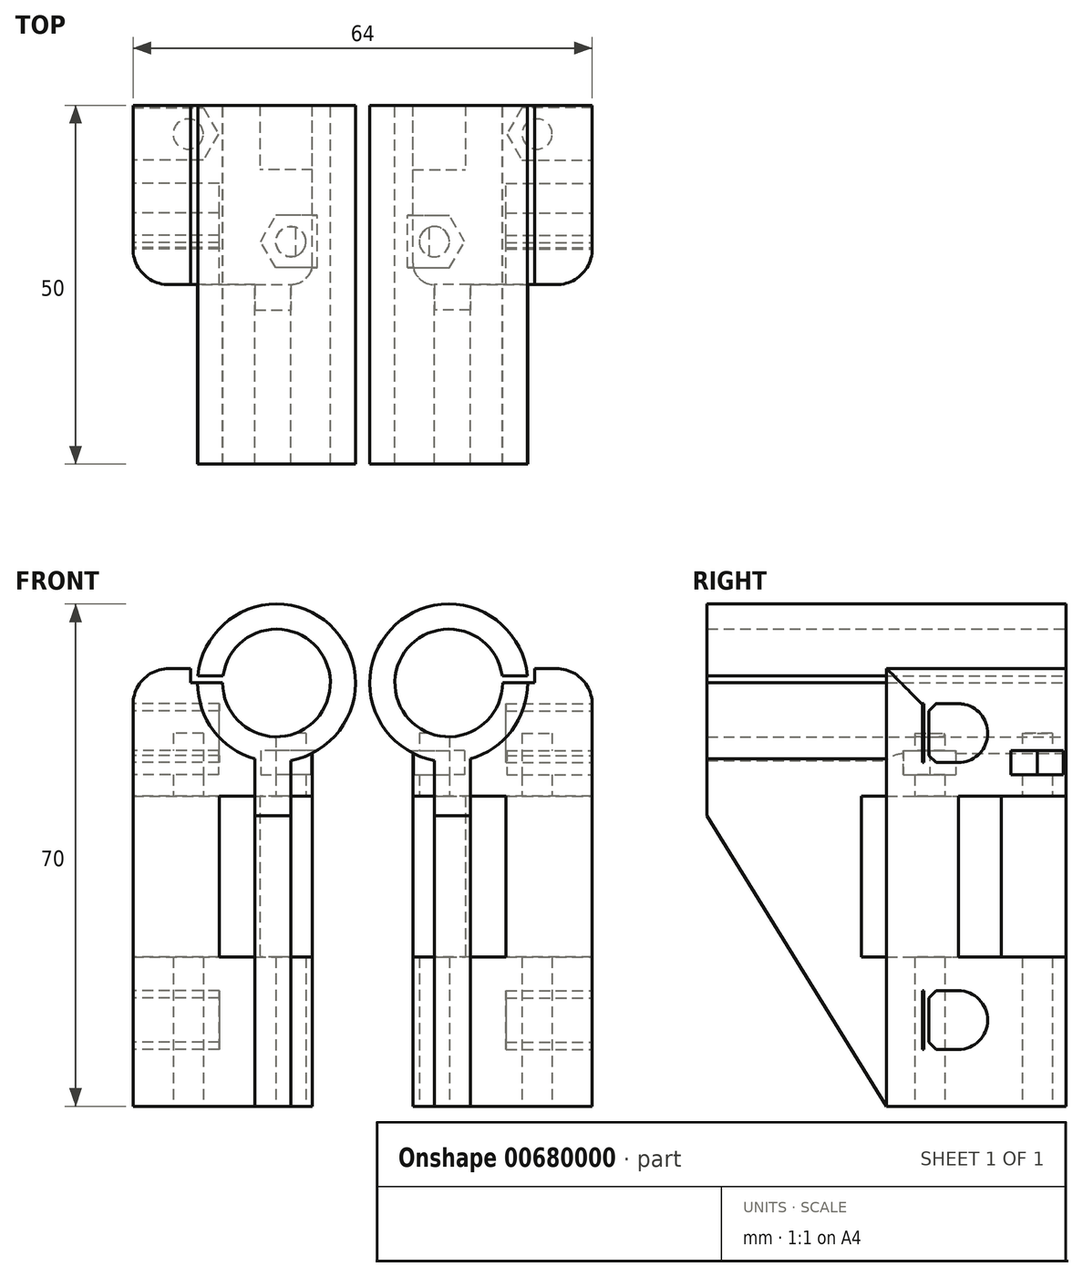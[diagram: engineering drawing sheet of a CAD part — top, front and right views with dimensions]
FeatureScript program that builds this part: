
annotation { "Feature Type Name" : "Feature", "Feature Type Description" : "" }
export const myFeature = defineFeature(function(context is Context, id is Id, definition is map)
    precondition{}
    {
        {
            var Q0;
            Q0=qCreatedBy(makeId("Front.planeOp"),FACE);
            var sketch = newSketch(context, id + "F0", { "sketchPlane" : qUnion([Q0])});
            skCircle(sketch, "E0", {"center": v(12, -12) * mm, "radius": 7.5 * mm});
            skCircle(sketch, "E1", {"center": v(12, -12) * mm, "radius": 11 * mm});
            skLineSegment(sketch, "E2", {"start": v(12, -12) * mm, "end": v(23, -12) * mm});
            skPoint(sketch, "E3.rect.middle", {"position": v(32, -10) * mm});
            skLineSegment(sketch, "E4", {"start": v(32, -10) * mm, "end": v(24, -10) * mm});
            skLineSegment(sketch, "E5", {"start": v(23, -12) * mm, "end": v(24, -12) * mm});
            skLineSegment(sketch, "E6", {"start": v(24, -12) * mm, "end": v(24, -10) * mm});
            skLineSegment(sketch, "E7", {"start": v(12, -12) * mm, "end": v(12, -11) * mm});
            skLineSegment(sketch, "E8", {"start": v(12, -11) * mm, "end": v(22.95, -11) * mm});
            skLineSegment(sketch, "E9", {"start": v(32, -10) * mm, "end": v(32, -71) * mm});
            skLineSegment(sketch, "E10", {"start": v(32, -71) * mm, "end": v(7, -71) * mm});
            skLineSegment(sketch, "E11", {"start": v(7, -71) * mm, "end": v(7, -23) * mm});
            skLineSegment(sketch, "E12", {"start": v(7, -23) * mm, "end": v(12, -23) * mm, "construction": true});
            skLineSegment(sketch, "E13", {"start": v(7, -23) * mm, "end": v(7, -21.8) * mm});
            skSolve(sketch);
        }
        {
            var Q0;
            {var subQ0=sQuery(id+"F0.wireOp",EDGE,"E2");var subQ1=sQuery(id+"F0.wireOp",EDGE,"E0");var subQ2=makeQuery(id+"F0.imprint","INTERSECT",VERTEX,{"derivedFrom":[subQ1,subQ0]});Q0=makeQuery(id+"F0.imprint","IMPRINT",FACE,{"disambiguationData":[TD([[makeQuery(id+"F0.imprint","IMPRINT",EDGE,{"disambiguationData":[TD([[subQ2,1.0]])],"derivedFrom":subQ1}),-1.0]])]});}
            extrude(context, id + "F1", {"entities" : qUnion([Q0]), "depth" : 50 * mm});
        }
        {
            var Q0;
            Q0=makeQuery(id+"F0.imprint","IMPRINT",FACE,{"disambiguationData":[TD([[makeQuery(id+"F0.imprint","IMPRINT",EDGE,{"derivedFrom":sQuery(id+"F0.wireOp",EDGE,"E4")}),1.0]])]});
            extrude(context, id + "F2", {"entities" : qUnion([Q0]), "operationType" : NewBodyOperationType.ADD, "depth" : 25 * mm});
        }
        {
            var Q0;
            Q0=makeQuery(id+"F2.opExtrude","SWEPT_FACE",FACE,{"disambiguationData":[OSD([sQuery(id+"F0.wireOp",EDGE,"E9")])]});
            var sketch = newSketch(context, id + "F3", { "sketchPlane" : qUnion([Q0])});
            skLineSegment(sketch, "E14", {"start": v(0, -71) * mm, "end": v(-15, -71) * mm, "construction": true});
            skLineSegment(sketch, "E15", {"start": v(-15, -71) * mm, "end": v(-15, -59) * mm, "construction": true});
            skLineSegment(sketch, "E16", {"start": v(-15, -59) * mm, "end": v(-15, -19) * mm, "construction": true});
            skCircle(sketch, "E17", {"center": v(-15, -59) * mm, "radius": 4.1 * mm});
            skCircle(sketch, "E18", {"center": v(-15, -59) * mm, "radius": 7.5 * mm, "construction": true});
            skCircle(sketch, "E19", {"center": v(-15, -19) * mm, "radius": 7.5 * mm, "construction": true});
            skLineSegment(sketch, "E20", {"start": v(-15, -39) * mm, "end": v(-16.5, -39) * mm, "construction": true});
            skLineSegment(sketch, "E21", {"start": v(-16.5, -39) * mm, "end": v(-16.5, -44.4) * mm, "construction": true});
            skCircle(sketch, "E22", {"center": v(-16.5, -44.4) * mm, "radius": 3 * mm, "construction": true});
            skCircle(sketch, "E23.0.MirrorC", {"center": v(-16.5, -33.6) * mm, "radius": 3 * mm, "construction": true});
            skLineSegment(sketch, "E24", {"start": v(-15, -54.9) * mm, "end": v(-20, -54.9) * mm, "construction": true});
            skLineSegment(sketch, "E25", {"start": v(-15, -63.1) * mm, "end": v(-20, -63.1) * mm, "construction": true});
            skLineSegment(sketch, "E26", {"start": v(-19.1, -54.9) * mm, "end": v(-19.1, -63.1) * mm});
            skLineSegment(sketch, "E27", {"start": v(-19.1, -55.9) * mm, "end": v(-18.1, -54.9) * mm});
            skLineSegment(sketch, "E28", {"start": v(-18.1, -54.9) * mm, "end": v(-15, -54.9) * mm});
            skLineSegment(sketch, "E29", {"start": v(-15, -63.1) * mm, "end": v(-18.1, -63.1) * mm});
            skLineSegment(sketch, "E30", {"start": v(-18.1, -63.1) * mm, "end": v(-19.1, -62.1) * mm});
            skLineSegment(sketch, "E31.bottom", {"start": v(-19.8, -54.9) * mm, "end": v(-20, -54.9) * mm});
            skLineSegment(sketch, "E31.top", {"start": v(-19.8, -63.1) * mm, "end": v(-20, -63.1) * mm});
            skLineSegment(sketch, "E31.left", {"start": v(-19.8, -54.9) * mm, "end": v(-19.8, -63.1) * mm});
            skLineSegment(sketch, "E31.right", {"start": v(-20, -54.9) * mm, "end": v(-20, -63.1) * mm});
            skLineSegment(sketch, "E32", {"start": v(-15, -39) * mm, "end": v(5.06, -39) * mm, "construction": true});
            skLineSegment(sketch, "E33.MirrorCS", {"start": v(-19.8, -23.1) * mm, "end": v(-20, -23.1) * mm});
            skLineSegment(sketch, "E34.MirrorCS", {"start": v(-19.8, -14.9) * mm, "end": v(-20, -14.9) * mm});
            skLineSegment(sketch, "E35.MirrorCS", {"start": v(-19.1, -22.1) * mm, "end": v(-18.1, -23.1) * mm});
            skLineSegment(sketch, "E36.MirrorCS", {"start": v(-18.1, -14.9) * mm, "end": v(-19.1, -15.9) * mm});
            skLineSegment(sketch, "E37.MirrorCS", {"start": v(-15, -14.9) * mm, "end": v(-20, -14.9) * mm, "construction": true});
            skLineSegment(sketch, "E38.MirrorCS", {"start": v(-15, -23.1) * mm, "end": v(-20, -23.1) * mm, "construction": true});
            skLineSegment(sketch, "E39.MirrorCS", {"start": v(-18.1, -23.1) * mm, "end": v(-15, -23.1) * mm});
            skLineSegment(sketch, "E40.MirrorCS", {"start": v(-19.8, -23.1) * mm, "end": v(-19.8, -14.9) * mm});
            skLineSegment(sketch, "E41.MirrorCS", {"start": v(-20, -23.1) * mm, "end": v(-20, -14.9) * mm});
            skLineSegment(sketch, "E42.MirrorCS", {"start": v(-19.1, -23.1) * mm, "end": v(-19.1, -14.9) * mm});
            skCircle(sketch, "E43.MirrorC", {"center": v(-15, -19) * mm, "radius": 4.1 * mm});
            skLineSegment(sketch, "E44.MirrorCS", {"start": v(-15, -14.9) * mm, "end": v(-18.1, -14.9) * mm});
            skSolve(sketch);
        }
        {
            var Q0;
            Q0=makeQuery(id+"F2.opExtrude","SWEPT_FACE",FACE,{"disambiguationData":[OSD([sQuery(id+"F0.wireOp",EDGE,"E10")])]});
            var sketch = newSketch(context, id + "F4", { "sketchPlane" : qUnion([Q0])});
            skLineSegment(sketch, "E45", {"start": v(0, 0) * mm, "end": v(0, 19) * mm, "construction": true});
            skLineSegment(sketch, "E46", {"start": v(0, 19) * mm, "end": v(10, 19) * mm, "construction": true});
            skLineSegment(sketch, "E47", {"start": v(10, 19) * mm, "end": v(10, 4) * mm, "construction": true});
            skLineSegment(sketch, "E48", {"start": v(10, 4) * mm, "end": v(24.3, 4) * mm, "construction": true});
            skCircle(sketch, "E49", {"center": v(10, 19) * mm, "radius": 2.1 * mm});
            skCircle(sketch, "E50", {"center": v(10, 19) * mm, "radius": 6.5 * mm, "construction": true});
            skCircle(sketch, "E51", {"center": v(24.3, 4) * mm, "radius": 2.1 * mm});
            skCircle(sketch, "E52", {"center": v(24.3, 4) * mm, "radius": 6.5 * mm, "construction": true});
            skLineSegment(sketch, "E53", {"start": v(14.3, 0) * mm, "end": v(14.3, 9) * mm});
            skLineSegment(sketch, "E54", {"start": v(20, 15) * mm, "end": v(32, 15) * mm});
            skLineSegment(sketch, "E55", {"start": v(32, 15) * mm, "end": v(32, 4) * mm});
            skLineSegment(sketch, "E56", {"start": v(24.3, 4) * mm, "end": v(24.3, 0) * mm, "construction": true});
            skLineSegment(sketch, "E57", {"start": v(24.3, 0) * mm, "end": v(14.3, 0) * mm});
            skLineSegment(sketch, "E58", {"start": v(20, 25) * mm, "end": v(20, 15) * mm});
            skLineSegment(sketch, "E59", {"start": v(7, 9) * mm, "end": v(14.3, 9) * mm});
            skLineSegment(sketch, "E60", {"start": v(7, 9) * mm, "end": v(7, 25) * mm});
            skLineSegment(sketch, "E61", {"start": v(7, 25) * mm, "end": v(20, 25) * mm});
            skLineSegment(sketch, "E62", {"start": v(24.3, 0) * mm, "end": v(32, 0) * mm});
            skLineSegment(sketch, "E63", {"start": v(32, 0) * mm, "end": v(32, 4) * mm});
            skLineSegment(sketch, "E64", {"start": v(32, 4) * mm, "end": v(24.3, 4) * mm, "construction": true});
            skSolve(sketch);
        }
        {
            var Q0;
            Q0=makeQuery(id+"F4.imprint","IMPRINT",FACE,{"disambiguationData":[TD([[makeQuery(id+"F4.imprint","IMPRINT",EDGE,{"derivedFrom":sQuery(id+"F4.wireOp",EDGE,"E49")}),-1.0]])]});
            extrude(context, id + "F5", {"entities" : qUnion([Q0]), "operationType" : NewBodyOperationType.REMOVE, "oppositeDirection" : true, "depth" : 12 * mm + (40 * mm + 22.4 * mm) * .5});
        }
        {
            var Q0;
            Q0=makeQuery(id+"F4.imprint","IMPRINT",FACE,{"disambiguationData":[TD([[makeQuery(id+"F4.imprint","IMPRINT",EDGE,{"derivedFrom":sQuery(id+"F4.wireOp",EDGE,"E49")}),-1.0]])]});
            extrude(context, id + "F6", {"entities" : qUnion([Q0]), "operationType" : NewBodyOperationType.ADD, "oppositeDirection" : true, "depth" : 12 * mm + (40 * mm - 22.4 * mm) * .5});
        }
        {
            var Q0;
            Q0=makeQuery(id+"F4.imprint","IMPRINT",FACE,{"disambiguationData":[TD([[makeQuery(id+"F4.imprint","IMPRINT",EDGE,{"derivedFrom":sQuery(id+"F4.wireOp",EDGE,"E49")}),1.0]])]});
            var Q1;
            Q1=makeQuery(id+"F4.imprint","IMPRINT",FACE,{"disambiguationData":[TD([[makeQuery(id+"F4.imprint","IMPRINT",EDGE,{"derivedFrom":sQuery(id+"F4.wireOp",EDGE,"E51")}),1.0]])]});
            extrude(context, id + "F7", {"entities" : qUnion([Q0, Q1]), "operationType" : NewBodyOperationType.REMOVE, "oppositeDirection" : true, "depth" : 12 * mm + 40 * mm});
        }
        {
            var Q0;
            Q0=makeQuery(id+"F5.boolean.opBoolean","COPY",FACE,{"derivedFrom":makeQuery(id+"F5.opExtrude","CAP_FACE",FACE,{"disambiguationData":[OSD([sQuery(id+"F4.wireOp",EDGE,"E49"),sQuery(id+"F4.wireOp",EDGE,"E51"),sQuery(id+"F4.wireOp",EDGE,"E53"),sQuery(id+"F4.wireOp",EDGE,"E54"),sQuery(id+"F4.wireOp",EDGE,"E55"),sQuery(id+"F4.wireOp",EDGE,"E57"),sQuery(id+"F4.wireOp",EDGE,"E58"),sQuery(id+"F4.wireOp",EDGE,"E59"),sQuery(id+"F4.wireOp",EDGE,"E60"),sQuery(id+"F4.wireOp",EDGE,"E61"),sQuery(id+"F4.wireOp",EDGE,"E62"),sQuery(id+"F4.wireOp",EDGE,"E63")])],"isStart":false})});
            var sketch = newSketch(context, id + "F8", { "sketchPlane" : qUnion([Q0])});
            skCircle(sketch, "E65.cCircle", {"center": v(24.3, 4) * mm, "radius": 3.65 * mm, "construction": true});
            skLineSegment(sketch, "E65.0", {"start": v(28.51, 4) * mm, "end": v(26.4, 0.35) * mm, "construction": true});
            skLineSegment(sketch, "E65.1", {"start": v(26.4, 0.35) * mm, "end": v(22.2, 0.35) * mm});
            skLineSegment(sketch, "E65.2", {"start": v(22.2, 0.35) * mm, "end": v(20.09, 4) * mm});
            skLineSegment(sketch, "E65.3", {"start": v(20.09, 4) * mm, "end": v(22.2, 7.65) * mm});
            skLineSegment(sketch, "E65.4", {"start": v(22.2, 7.65) * mm, "end": v(26.4, 7.65) * mm});
            skLineSegment(sketch, "E65.5", {"start": v(26.4, 7.65) * mm, "end": v(28.51, 4) * mm, "construction": true});
            skPoint(sketch, "E65.0.midPoint", {"position": v(27.46, 2.18) * mm});
            skCircle(sketch, "E66.cCircle", {"center": v(10, 19) * mm, "radius": 3.65 * mm, "construction": true});
            skLineSegment(sketch, "E66.0", {"start": v(14.21, 19) * mm, "end": v(12.1, 15.35) * mm});
            skLineSegment(sketch, "E66.1", {"start": v(12.1, 15.35) * mm, "end": v(7.9, 15.35) * mm});
            skLineSegment(sketch, "E66.2", {"start": v(7.9, 15.35) * mm, "end": v(5.79, 19) * mm, "construction": true});
            skLineSegment(sketch, "E66.3", {"start": v(5.79, 19) * mm, "end": v(7.9, 22.65) * mm, "construction": true});
            skLineSegment(sketch, "E66.4", {"start": v(7.9, 22.65) * mm, "end": v(12.1, 22.65) * mm});
            skLineSegment(sketch, "E66.5", {"start": v(12.1, 22.65) * mm, "end": v(14.21, 19) * mm});
            skPoint(sketch, "E66.0.midPoint", {"position": v(13.16, 17.18) * mm});
            skLineSegment(sketch, "E67", {"start": v(7.9, 22.65) * mm, "end": v(7, 22.65) * mm});
            skLineSegment(sketch, "E68", {"start": v(7, 22.65) * mm, "end": v(7, 15.35) * mm});
            skLineSegment(sketch, "E69", {"start": v(7, 15.35) * mm, "end": v(7.9, 15.35) * mm});
            skLineSegment(sketch, "E70", {"start": v(26.4, 7.65) * mm, "end": v(32, 7.65) * mm});
            skLineSegment(sketch, "E71", {"start": v(32, 7.65) * mm, "end": v(32, 0.35) * mm});
            skLineSegment(sketch, "E72", {"start": v(32, 0.35) * mm, "end": v(26.4, 0.35) * mm});
            skLineSegment(sketch, "E73", {"start": v(7, 22.65) * mm, "end": v(-3, 22.65) * mm});
            skLineSegment(sketch, "E74", {"start": v(-3, 22.65) * mm, "end": v(-3, 15.35) * mm});
            skLineSegment(sketch, "E75", {"start": v(-3, 15.35) * mm, "end": v(7, 15.35) * mm});
            skSolve(sketch);
        }
        {
            var Q0;
            Q0=makeQuery(id+"F8.imprint","IMPRINT",FACE,{"disambiguationData":[TD([[makeQuery(id+"F8.imprint","IMPRINT",EDGE,{"derivedFrom":sQuery(id+"F8.wireOp",EDGE,"E65.1")}),-1.0]])]});
            var Q1;
            Q1=makeQuery(id+"F8.imprint","IMPRINT",FACE,{"disambiguationData":[TD([[makeQuery(id+"F8.imprint","IMPRINT",EDGE,{"derivedFrom":sQuery(id+"F8.wireOp",EDGE,"E66.0")}),-1.0]])]});
            var Q2;
            Q2=makeQuery(id+"F8.imprint","IMPRINT",FACE,{"disambiguationData":[TD([[makeQuery(id+"F8.imprint","IMPRINT",EDGE,{"derivedFrom":sQuery(id+"F8.wireOp",EDGE,"E68")}),-1.0]])]});
            extrude(context, id + "F9", {"entities" : qUnion([Q0, Q1, Q2]), "operationType" : NewBodyOperationType.REMOVE, "oppositeDirection" : true, "depth" : 6.4 * mm});
        }
        {
            var Q0;
            Q0=makeQuery(id+"F8.imprint","IMPRINT",FACE,{"disambiguationData":[TD([[makeQuery(id+"F8.imprint","IMPRINT",EDGE,{"derivedFrom":sQuery(id+"F8.wireOp",EDGE,"E66.0")}),-1.0]])]});
            var Q1;
            Q1=makeQuery(id+"F8.imprint","IMPRINT",FACE,{"disambiguationData":[TD([[makeQuery(id+"F8.imprint","IMPRINT",EDGE,{"derivedFrom":sQuery(id+"F8.wireOp",EDGE,"E65.1")}),-1.0]])]});
            extrude(context, id + "F10", {"entities" : qUnion([Q0, Q1]), "operationType" : NewBodyOperationType.ADD, "oppositeDirection" : true, "depth" : 3 * mm});
        }
        {
            var Q0;
            Q0=qSketchRegion(id+"F3",true);
            extrude(context, id + "F11", {"entities" : qUnion([Q0]), "operationType" : NewBodyOperationType.REMOVE, "oppositeDirection" : true, "depth" : 12 * mm});
        }
        {
            var Q0;
            Q0=makeQuery(id+"F10.boolean.opBoolean","MERGE",FACE,{"derivedFrom":[makeQuery(id+"F6.boolean.opBoolean","MERGE",FACE,{"derivedFrom":[makeQuery(id+"F2.opExtrude","SWEPT_FACE",FACE,{"disambiguationData":[OSD([sQuery(id+"F0.wireOp",EDGE,"E11"),sQuery(id+"F0.wireOp",EDGE,"E13")])]}),makeQuery(id+"F6.opExtrude","SWEPT_FACE",FACE,{"disambiguationData":[OSD([sQuery(id+"F4.wireOp",EDGE,"E60")])]})]}),makeQuery(id+"F10.opExtrude","SWEPT_FACE",FACE,{"disambiguationData":[OSD([sQuery(id+"F8.wireOp",EDGE,"E68")])]})]});
            cPlane(context, id + "F12", {"entities" : qUnion([Q0]), "cplaneType" : CPlaneType.OFFSET, "offset" : 3 * mm, "oppositeDirection" : true, "width" : 150 * mm, "height" : 150 * mm});
        }
        {
            var Q0;
            Q0=qCreatedBy(id+"F12.planeOp",FACE);
            var sketch = newSketch(context, id + "F13", { "sketchPlane" : qUnion([Q0])});
            skLineSegment(sketch, "E76.0.0", {"start": v(9, -50.2) * mm, "end": v(9, -27.8) * mm});
            skLineSegment(sketch, "E76.0.1", {"start": v(9, -27.8) * mm, "end": v(25, -27.8) * mm});
            skLineSegment(sketch, "E76.0.2", {"start": v(25, -27.8) * mm, "end": v(25, -21.8) * mm});
            skLineSegment(sketch, "E76.0.4", {"start": v(0, -21.8) * mm, "end": v(0, -71) * mm});
            skLineSegment(sketch, "E76.0.5", {"start": v(0, -71) * mm, "end": v(25, -71) * mm});
            skLineSegment(sketch, "E76.0.6", {"start": v(25, -71) * mm, "end": v(25, -50.2) * mm});
            skLineSegment(sketch, "E76.0.7", {"start": v(25, -50.2) * mm, "end": v(9, -50.2) * mm});
            skLineSegment(sketch, "E77", {"start": v(25, -27.8) * mm, "end": v(28.5, -27.8) * mm});
            skLineSegment(sketch, "E78", {"start": v(28.5, -27.8) * mm, "end": v(28.5, -50.2) * mm});
            skLineSegment(sketch, "E79", {"start": v(28.5, -50.2) * mm, "end": v(25, -50.2) * mm});
            skLineSegment(sketch, "E80.0", {"start": v(50, -1) * mm, "end": v(50, -23) * mm});
            skLineSegment(sketch, "E81", {"start": v(25, -20.5) * mm, "end": v(25, -21.8) * mm});
            skLineSegment(sketch, "E82", {"start": v(25, -20.5) * mm, "end": v(50, -20.5) * mm});
            skLineSegment(sketch, "E83", {"start": v(50, -20.5) * mm, "end": v(50, -30.5) * mm});
            skLineSegment(sketch, "E84", {"start": v(50, -30.5) * mm, "end": v(25, -71) * mm});
            skLineSegment(sketch, "E85", {"start": v(43, -29) * mm, "end": v(43, -38.5) * mm, "construction": true});
            skCircle(sketch, "E86", {"center": v(43, -29) * mm, "radius": 1.05 * mm, "construction": true});
            skCircle(sketch, "E87", {"center": v(43, -38.5) * mm, "radius": 1.05 * mm, "construction": true});
            skPoint(sketch, "E88.0", {"position": v(0, -12) * mm});
            skSolve(sketch);
        }
        {
            var Q0;
            Q0=makeQuery(id+"F13.imprint","IMPRINT",FACE,{"disambiguationData":[TD([[makeQuery(id+"F13.imprint","IMPRINT",EDGE,{"derivedFrom":sQuery(id+"F13.wireOp",EDGE,"E76.0.2")}),-1.0]])]});
            extrude(context, id + "F14", {"entities" : qUnion([Q0]), "operationType" : NewBodyOperationType.ADD, "oppositeDirection" : true, "depth" : 5 * mm});
        }
        {
            var Q0;
            {var subQ0=sQuery(id+"F0.wireOp",EDGE,"E1");var subQ1=sQuery(id+"F0.wireOp",EDGE,"E4");var subQ2=sQuery(id+"F0.wireOp",EDGE,"E5");var subQ3=sQuery(id+"F0.wireOp",EDGE,"E6");var subQ4=sQuery(id+"F0.wireOp",EDGE,"E9");var subQ5=sQuery(id+"F0.wireOp",EDGE,"E10");var subQ6=sQuery(id+"F4.wireOp",EDGE,"E61");var subQ7=sQuery(id+"F13.wireOp",EDGE,"E77");var subQ8=sQuery(id+"F8.wireOp",EDGE,"E71");var subQ9=sQuery(id+"F4.wireOp",EDGE,"E49");var subQ10=sQuery(id+"F4.wireOp",EDGE,"E51");var subQ11=sQuery(id+"F13.wireOp",EDGE,"E79");var subQ12=sQuery(id+"F13.wireOp",EDGE,"E84");var subQ13=sQuery(id+"F4.wireOp",EDGE,"E53");var subQ14=sQuery(id+"F4.wireOp",EDGE,"E54");var subQ15=sQuery(id+"F4.wireOp",EDGE,"E55");var subQ16=sQuery(id+"F4.wireOp",EDGE,"E57");var subQ17=sQuery(id+"F4.wireOp",EDGE,"E58");var subQ18=sQuery(id+"F4.wireOp",EDGE,"E59");var subQ19=sQuery(id+"F4.wireOp",EDGE,"E60");var subQ20=sQuery(id+"F4.wireOp",EDGE,"E62");var subQ21=sQuery(id+"F4.wireOp",EDGE,"E63");Q0=makeQuery(id+"F14.boolean.opBoolean","SPLIT",FACE,{"disambiguationData":[TD([makeQuery(id+"F1.opExtrude","SWEPT_FACE",FACE,{"disambiguationData":[OSD([subQ0])]}),makeQuery(id+"F1.opExtrude","SWEPT_FACE",FACE,{"disambiguationData":[OSD([sQuery(id+"F0.wireOp",EDGE,"E2")])]}),makeQuery(id+"F2.opExtrude","SWEPT_FACE",FACE,{"disambiguationData":[OSD([subQ1])]}),makeQuery(id+"F2.opExtrude","SWEPT_FACE",FACE,{"disambiguationData":[OSD([subQ2])]}),makeQuery(id+"F2.opExtrude","SWEPT_FACE",FACE,{"disambiguationData":[OSD([subQ3])]}),makeQuery(id+"F2.opExtrude","SWEPT_FACE",FACE,{"disambiguationData":[OSD([subQ4])]}),makeQuery(id+"F2.opExtrude","SWEPT_FACE",FACE,{"disambiguationData":[OSD([subQ5])]}),makeQuery(id+"F5.boolean.opBoolean","COPY",FACE,{"derivedFrom":makeQuery(id+"F5.opExtrude","CAP_FACE",FACE,{"disambiguationData":[OSD([subQ9,subQ10,subQ13,subQ14,subQ15,subQ16,subQ17,subQ18,subQ19,subQ6,subQ20,subQ21])],"isStart":false})}),makeQuery(id+"F5.boolean.opBoolean","COPY",FACE,{"derivedFrom":makeQuery(id+"F5.opExtrude","SWEPT_FACE",FACE,{"disambiguationData":[OSD([subQ17])]})}),makeQuery(id+"F6.opExtrude","CAP_FACE",FACE,{"disambiguationData":[OSD([subQ9,subQ10,subQ13,subQ14,subQ15,subQ16,subQ17,subQ18,subQ19,subQ6,subQ20,subQ21])],"isStart":true}),makeQuery(id+"F6.opExtrude","CAP_FACE",FACE,{"disambiguationData":[OSD([subQ9,subQ10,subQ13,subQ14,subQ15,subQ16,subQ17,subQ18,subQ19,subQ6,subQ20,subQ21])],"isStart":false}),makeQuery(id+"F6.opExtrude","SWEPT_FACE",FACE,{"disambiguationData":[OSD([subQ15,subQ21])]}),makeQuery(id+"F10.opExtrude","CAP_FACE",FACE,{"disambiguationData":[OSD([subQ10,sQuery(id+"F8.wireOp",EDGE,"E65.1"),sQuery(id+"F8.wireOp",EDGE,"E65.2"),sQuery(id+"F8.wireOp",EDGE,"E65.3"),sQuery(id+"F8.wireOp",EDGE,"E65.4"),sQuery(id+"F8.wireOp",EDGE,"E70"),subQ8,sQuery(id+"F8.wireOp",EDGE,"E72")])],"isStart":true}),makeQuery(id+"F10.opExtrude","CAP_FACE",FACE,{"disambiguationData":[OSD([subQ9,sQuery(id+"F8.wireOp",EDGE,"E66.0"),sQuery(id+"F8.wireOp",EDGE,"E66.1"),sQuery(id+"F8.wireOp",EDGE,"E66.4"),sQuery(id+"F8.wireOp",EDGE,"E66.5"),sQuery(id+"F8.wireOp",EDGE,"E67"),sQuery(id+"F8.wireOp",EDGE,"E68"),sQuery(id+"F8.wireOp",EDGE,"E69")])],"isStart":true}),makeQuery(id+"F10.opExtrude","SWEPT_FACE",FACE,{"disambiguationData":[OSD([subQ8])]}),makeQuery(id+"F14.opExtrude","CAP_FACE",FACE,{"disambiguationData":[OSD([sQuery(id+"F13.wireOp",EDGE,"E76.0.2"),sQuery(id+"F13.wireOp",EDGE,"E76.0.6"),subQ7,sQuery(id+"F13.wireOp",EDGE,"E78"),subQ11,sQuery(id+"F13.wireOp",EDGE,"E82"),sQuery(id+"F13.wireOp",EDGE,"E83"),subQ12,sQuery(id+"F13.wireOp",EDGE,"E86"),sQuery(id+"F13.wireOp",EDGE,"E87")])],"isStart":false}),makeQuery(id+"F14.opExtrude","SWEPT_FACE",FACE,{"disambiguationData":[OSD([subQ7])]}),makeQuery(id+"F14.opExtrude","SWEPT_FACE",FACE,{"disambiguationData":[OSD([subQ11])]}),makeQuery(id+"F14.opExtrude","SWEPT_FACE",FACE,{"disambiguationData":[OSD([subQ12])]})])],"derivedFrom":makeQuery(id+"F6.boolean.opBoolean","MERGE",FACE,{"derivedFrom":[makeQuery(id+"F2.opExtrude","CAP_FACE",FACE,{"disambiguationData":[OSD([subQ0,subQ1,subQ2,subQ3,subQ4,subQ5,sQuery(id+"F0.wireOp",EDGE,"E11"),sQuery(id+"F0.wireOp",EDGE,"E13")])],"isStart":false}),makeQuery(id+"F6.opExtrude","SWEPT_FACE",FACE,{"disambiguationData":[OSD([subQ6])]})]})});}
            var sketch = newSketch(context, id + "F15", { "sketchPlane" : qUnion([Q0])});
            skLineSegment(sketch, "E89", {"start": v(25, -28) * mm, "end": v(25, -37.5) * mm, "construction": true});
            skCircle(sketch, "E90", {"center": v(25, -37.5) * mm, "radius": 1.05 * mm});
            skCircle(sketch, "E91", {"center": v(25, -28) * mm, "radius": 1.05 * mm});
            skSolve(sketch);
        }
        {
            var Q0;
            Q0=qCreatedBy(makeId("Right.planeOp"),FACE);
            var Q1;
            Q1=sQuery(id+"F0.wireOp",VERTEX,"E1.center");
            cPlane(context, id + "F16", {"entities" : qUnion([Q0, Q1]), "cplaneType" : CPlaneType.PLANE_POINT, "offset" : 150 * mm, "width" : 150 * mm, "height" : 150 * mm});
        }
        {
            var Q0;
            Q0=qCreatedBy(id+"F16.planeOp",FACE);
            var sketch = newSketch(context, id + "F17", { "sketchPlane" : qUnion([Q0])});
            skPoint(sketch, "E92.0", {"position": v(0, -12) * mm});
            skLineSegment(sketch, "E93.0", {"start": v(0, -19.5) * mm, "end": v(0, -4.5) * mm});
            skLineSegment(sketch, "E94.0", {"start": v(-50, -19.5) * mm, "end": v(-50, -4.5) * mm});
            skLineSegment(sketch, "E95", {"start": v(0, -12) * mm, "end": v(-50, -12) * mm});
            skArc(sketch, "E96", {"start": v(-2, -19.27) * mm, "mid": v(-10, -18) * mm, "end": v(-18, -19.27) * mm});
            skLineSegment(sketch, "E97", {"start": v(-2, -4.73) * mm, "end": v(-18, -4.73) * mm, "construction": true});
            skLineSegment(sketch, "E98", {"start": v(-2, -19.27) * mm, "end": v(0.34, -20.03) * mm, "construction": true});
            skLineSegment(sketch, "E99", {"start": v(-10, -43.89) * mm, "end": v(-10, -12) * mm, "construction": true});
            skArc(sketch, "E100", {"start": v(-2, -19.27) * mm, "mid": v(-0.85, -12) * mm, "end": v(-2, -4.73) * mm});
            skArc(sketch, "E101", {"start": v(-18, -4.73) * mm, "mid": v(-19.15, -12) * mm, "end": v(-18, -19.27) * mm});
            skLineSegment(sketch, "E102", {"start": v(-2, -19.27) * mm, "end": v(-2.8, -21.7) * mm, "construction": true});
            skPoint(sketch, "E103", {"position": v(-10, -18) * mm});
            skLineSegment(sketch, "E104", {"start": v(-25, -12) * mm, "end": v(-25, -25.7) * mm, "construction": true});
            skArc(sketch, "E105.0.MirrorCS", {"start": v(-32, -4.73) * mm, "mid": v(-30.85, -12) * mm, "end": v(-32, -19.27) * mm});
            skArc(sketch, "E105.1.MirrorCS", {"start": v(-48, -19.27) * mm, "mid": v(-40, -18) * mm, "end": v(-32, -19.27) * mm});
            skArc(sketch, "E105.2.MirrorCS", {"start": v(-48, -19.27) * mm, "mid": v(-49.15, -12) * mm, "end": v(-48, -4.73) * mm});
            skSolve(sketch);
        }
        {
            var Q0;
            Q0=makeQuery(id+"F2.opExtrude","CAP_EDGE",EDGE,{"disambiguationData":[OSD([sQuery(id+"F0.wireOp",EDGE,"E9")])],"isStart":false});
            var Q1;
            Q1=makeQuery(id+"F2.opExtrude","SWEPT_EDGE",EDGE,{"disambiguationData":[OSD([sQuery(id+"F0.wireOp",EDGE,"E4"),sQuery(id+"F0.wireOp",EDGE,"E9")])]});
            fillet(context, id + "F18", {"entities" : qUnion([Q0, Q1]), "radius" : 5 * mm, "tangentPropagation" : true, "allowEdgeOverflow" : false});
        }
        {
            var Q0;
            Q0=makeQuery(id+"F2.opExtrude","CAP_EDGE",EDGE,{"disambiguationData":[OSD([sQuery(id+"F0.wireOp",EDGE,"E11"),sQuery(id+"F0.wireOp",EDGE,"E13")])],"isStart":false});
            var Q1;
            Q1=makeQuery(id+"F6.opExtrude","SWEPT_EDGE",EDGE,{"disambiguationData":[OSD([sQuery(id+"F4.wireOp",EDGE,"E60"),sQuery(id+"F4.wireOp",EDGE,"E61")])]});
            fillet(context, id + "F19", {"entities" : qUnion([Q0, Q1]), "radius" : 3 * mm, "tangentPropagation" : true, "allowEdgeOverflow" : false});
        }
        {
            var Q0;
            Q0=makeQuery(id+"F1.opExtrude","SWEPT_BODY",BODY,{"disambiguationData":[OSD([sQuery(id+"F0.wireOp",EDGE,"E0"),sQuery(id+"F0.wireOp",EDGE,"E1"),sQuery(id+"F0.wireOp",EDGE,"E2"),sQuery(id+"F0.wireOp",EDGE,"E8")])]});
            var Q1;
            Q1=qCreatedBy(makeId("Right.planeOp"),FACE);
            mirror(context, id + "F20", {"entities" : qUnion([Q0]), "mirrorPlane" : qUnion([Q1])});
        }
    });
